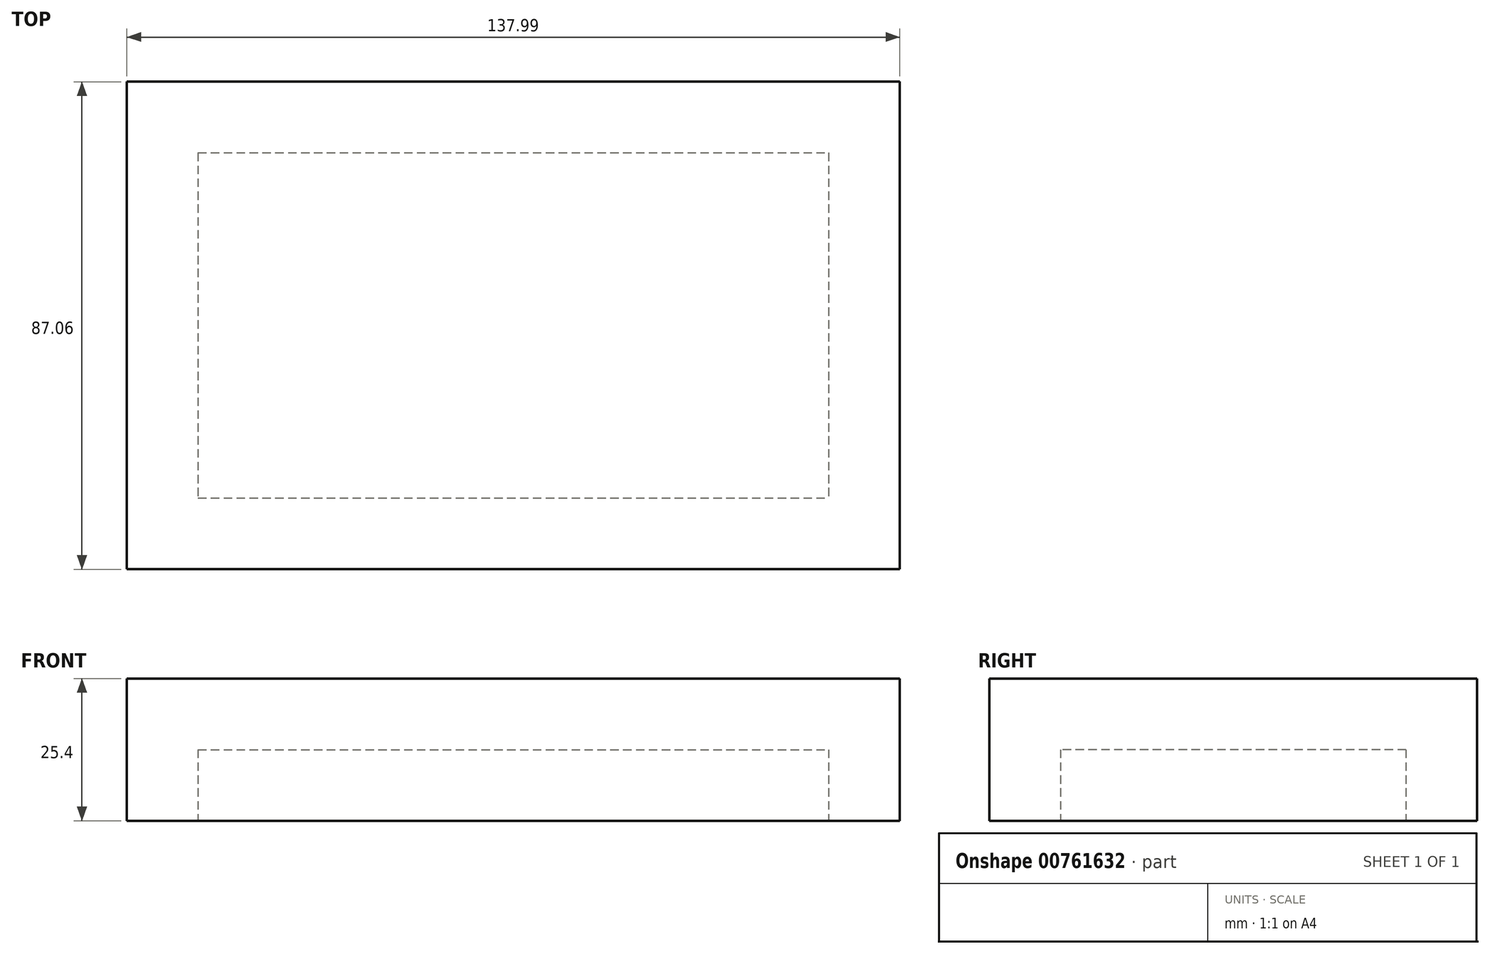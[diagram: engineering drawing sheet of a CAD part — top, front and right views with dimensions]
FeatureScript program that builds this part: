
annotation { "Feature Type Name" : "Feature", "Feature Type Description" : "" }
export const myFeature = defineFeature(function(context is Context, id is Id, definition is map)
    precondition{}
    {
        {
            var Q0;
            Q0=qCreatedBy(makeId("Top.planeOp"),FACE);
            var sketch = newSketch(context, id + "F0", { "sketchPlane" : qUnion([Q0])});
            skLineSegment(sketch, "E0.bottom", {"start": v(-70.45, 41.26) * mm, "end": v(67.54, 41.26) * mm});
            skLineSegment(sketch, "E0.top", {"start": v(-70.45, -45.8) * mm, "end": v(67.54, -45.8) * mm});
            skLineSegment(sketch, "E0.left", {"start": v(-70.45, 41.26) * mm, "end": v(-70.45, -45.8) * mm});
            skLineSegment(sketch, "E0.right", {"start": v(67.54, 41.26) * mm, "end": v(67.54, -45.8) * mm});
            skSolve(sketch);
        }
        {
            var Q0;
            Q0=makeQuery(id+"F0.imprint","IMPRINT",FACE,{"disambiguationData":[TD([[makeQuery(id+"F0.imprint","IMPRINT",EDGE,{"derivedFrom":sQuery(id+"F0.wireOp",EDGE,"E0.bottom")}),-1.0]])]});
            extrude(context, id + "F1", {"entities" : qUnion([Q0]), "depth" : 25.4 * mm, "offsetDistance" : 25.4 * mm});
        }
        {
            var Q0;
            Q0=makeQuery(id+"F1.opExtrude","CAP_FACE",FACE,{"disambiguationData":[OSD([sQuery(id+"F0.wireOp",EDGE,"E0.bottom"),sQuery(id+"F0.wireOp",EDGE,"E0.top"),sQuery(id+"F0.wireOp",EDGE,"E0.left"),sQuery(id+"F0.wireOp",EDGE,"E0.right")])],"isStart":true});
            shell(context, id + "F2", {"entities" : qUnion([Q0]), "thickness" : 12.7 * mm});
        }
    });
